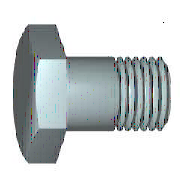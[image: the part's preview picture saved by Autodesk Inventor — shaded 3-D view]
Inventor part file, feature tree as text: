
AUTODESK INVENTOR PART (.ipt)
format: ipt  version: 2021 (Build 250183000, 183)  size: 198,144 bytes
history: native  units: mm (DEFAULTED — no unit token found)
features: sketch x4, other x4, plane x3, chamfer x1, fillet x1
ambient origin geometry x6: Origin, XY Plane, X Axis, Y Axis, Z Axis, Center Point
bodies: Solid1 (feature_tree)
feature tree (13):
  plane  "WorkPlane1"
  sketch  "Sketch1"  dims[d0=30.0mm]
  other  "WorkPoint1"
  chamfer  "Chamfer1"  Distance=4.0mm
  fillet  "Fillet1"  [1 undecoded]
  other  "MSC_A1"
  other  "MSC_PF1"
  other  "MSC_PT1"
  plane  "WorkPlane2"
  plane  "WorkPlane3"
  sketch  "Sketch2"  dims[d1=10.0mm]
  sketch  "Sketch3"  dims[d2=15.0mm]
  sketch  "Sketch4"  dims[d4=17.321016mm d6=4.0mm d7=0.0mm d8=15.0mm d10=0.0mm d12=30.0deg d14=360.0deg d15=0.0mm d17=10.0mm d18=3.0mm d19=80.0mm d20=60.0mm d21=360.0deg d22=0.5mm d23=0.5mm d24=0.25mm d25=0.1mm d26=0.0mm d27=60.0deg d28=5.0mm d29=0.0mm d30=0.0mm d32=0.0mm d33=0.0mm d34=0.0mm d37=0.0mm d38=0.0mm d39=45.0deg d40=0.0mm d41=0.0mm d42=0.0mm]
note: 1 required parameter value undecoded (feature->parameter linkage not recoverable at this tier; creation-order binding heuristic only, values carry confidence <= 0.55)
